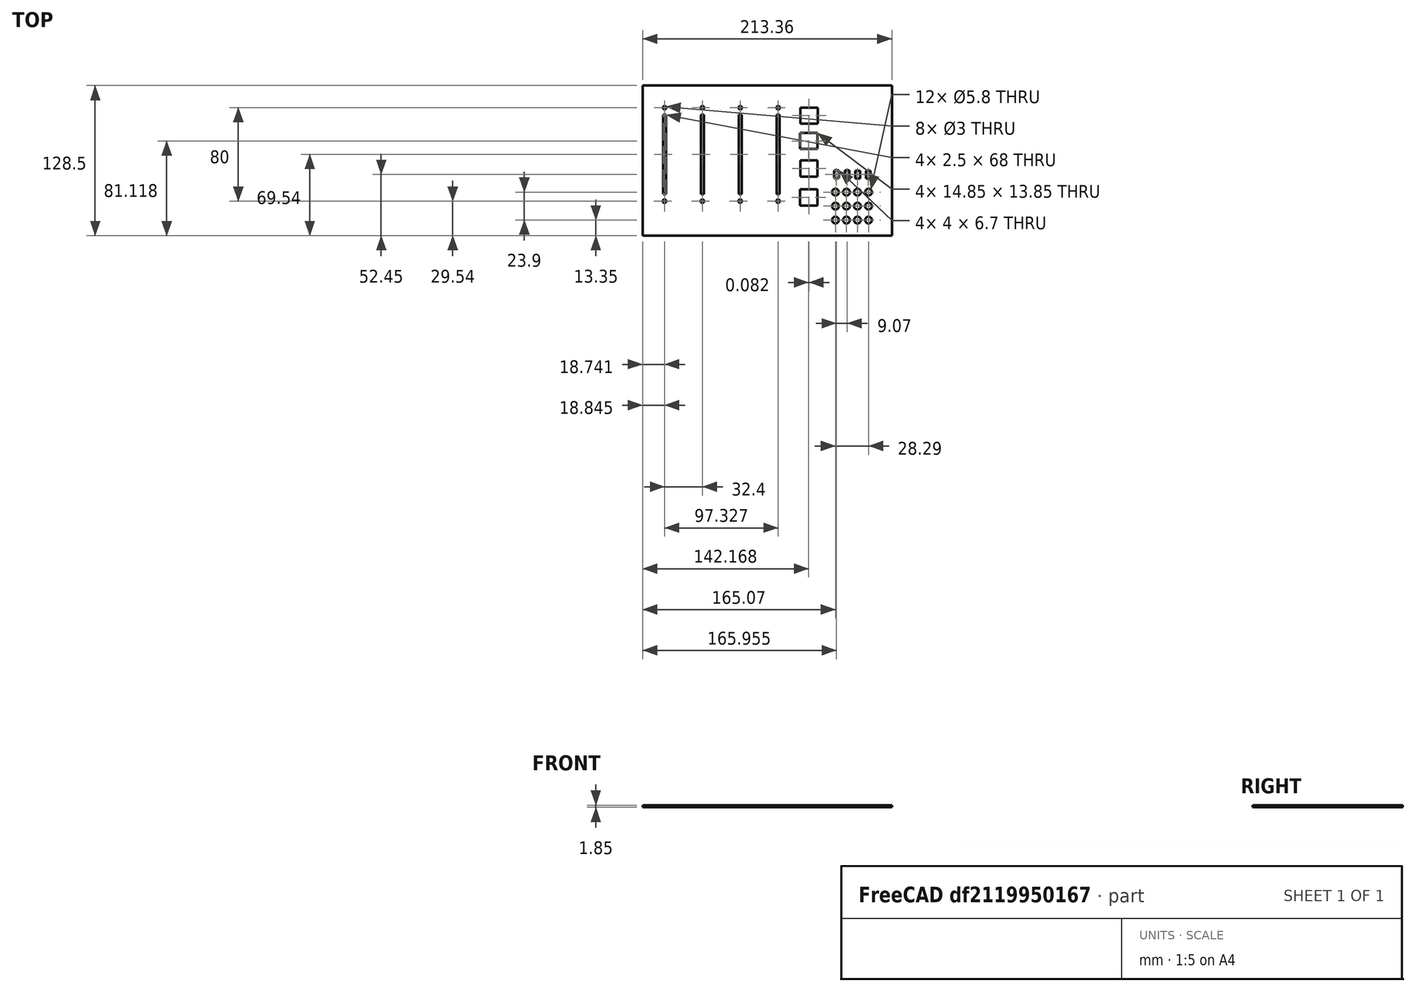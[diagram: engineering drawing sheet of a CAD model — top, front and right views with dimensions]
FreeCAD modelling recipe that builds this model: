
FCSTD DOCUMENT  (FreeCAD 0.19R24267 +148 (Git))
Label: FrontPanel
License: All rights reserved
LicenseURL: http://en.wikipedia.org/wiki/All_rights_reserved
objects: Sketcher::SketchObject×1, PartDesign::Pad×1, PartDesign::Body×1
note: 4 computed .brp shape members not serialized (recipe doc carries the construction recipe); baked Part::Feature solids carry a one-line shape summary decoded from their .brp

FEATURE [Sketcher::SketchObject] Sketch
  FullyConstrained = false
  MapMode = 5
  Support = -> [XY_Plane]
  sketch-geometry (93):
    g0: GeomPoint X=0 Y=0 Z=0
    g1: LineSegment StartX=0 StartY=0 StartZ=0 EndX=213.36 EndY=0 EndZ=0
    g2: LineSegment StartX=0 StartY=0 StartZ=0 EndX=0 EndY=128.5 EndZ=0
    g3: LineSegment StartX=0 StartY=128.5 StartZ=0 EndX=213.36 EndY=128.5 EndZ=0
    g4: LineSegment StartX=213.36 StartY=0 StartZ=0 EndX=213.36 EndY=128.5 EndZ=0
    g5: LineSegment StartX=17.5952 StartY=103.54 StartZ=0 EndX=20.0952 EndY=103.54 EndZ=0
    g6: LineSegment StartX=20.0952 StartY=103.54 StartZ=0 EndX=20.0952 EndY=35.54 EndZ=0
    g7: LineSegment StartX=20.0952 StartY=35.54 StartZ=0 EndX=17.5952 EndY=35.54 EndZ=0
    g8: LineSegment StartX=17.5952 StartY=35.54 StartZ=0 EndX=17.5952 EndY=103.54 EndZ=0
    g9: LineSegment StartX=49.9947 StartY=103.54 StartZ=0 EndX=52.4947 EndY=103.54 EndZ=0
    g10: LineSegment StartX=52.4947 StartY=103.54 StartZ=0 EndX=52.4947 EndY=35.54 EndZ=0
    g11: LineSegment StartX=52.4947 StartY=35.54 StartZ=0 EndX=49.9947 EndY=35.54 EndZ=0
    g12: LineSegment StartX=49.9947 StartY=35.54 StartZ=0 EndX=49.9947 EndY=103.54 EndZ=0
    g13: LineSegment StartX=17.5952 StartY=103.54 StartZ=0 EndX=49.9947 EndY=103.54 EndZ=0
    g14: LineSegment StartX=82.3943 StartY=103.54 StartZ=0 EndX=84.8943 EndY=103.54 EndZ=0
    g15: LineSegment StartX=84.8943 StartY=103.54 StartZ=0 EndX=84.8943 EndY=35.54 EndZ=0
    g16: LineSegment StartX=84.8943 StartY=35.54 StartZ=0 EndX=82.3943 EndY=35.54 EndZ=0
    g17: LineSegment StartX=82.3943 StartY=35.54 StartZ=0 EndX=82.3943 EndY=103.54 EndZ=0
    g18: LineSegment StartX=49.9947 StartY=103.54 StartZ=0 EndX=82.3943 EndY=103.54 EndZ=0
    g19: LineSegment StartX=114.794 StartY=103.54 StartZ=0 EndX=117.294 EndY=103.54 EndZ=0
    g20: LineSegment StartX=117.294 StartY=103.54 StartZ=0 EndX=117.294 EndY=35.54 EndZ=0
    g21: LineSegment StartX=117.294 StartY=35.54 StartZ=0 EndX=114.794 EndY=35.54 EndZ=0
    g22: LineSegment StartX=114.794 StartY=35.54 StartZ=0 EndX=114.794 EndY=103.54 EndZ=0
    g23: LineSegment StartX=82.3943 StartY=103.54 StartZ=0 EndX=114.794 EndY=103.54 EndZ=0
    g24: Circle CenterX=18.87 CenterY=109.54 CenterZ=0 NormalX=0 NormalY=0 NormalZ=1 AngleXU=0 Radius=1.5
    g25: Circle CenterX=18.7415 CenterY=29.54 CenterZ=0 NormalX=0 NormalY=0 NormalZ=1 AngleXU=0 Radius=1.5
    g26: Circle CenterX=51.141 CenterY=29.54 CenterZ=0 NormalX=0 NormalY=0 NormalZ=1 AngleXU=0 Radius=1.5
    g27: Circle CenterX=51.2695 CenterY=109.54 CenterZ=0 NormalX=0 NormalY=0 NormalZ=1 AngleXU=0 Radius=1.5
    g28: LineSegment StartX=18.7415 StartY=29.54 StartZ=0 EndX=51.141 EndY=29.54 EndZ=0
    g29: Circle CenterX=83.5405 CenterY=29.54 CenterZ=0 NormalX=0 NormalY=0 NormalZ=1 AngleXU=0 Radius=1.5
    g30: Circle CenterX=83.669 CenterY=109.54 CenterZ=0 NormalX=0 NormalY=0 NormalZ=1 AngleXU=0 Radius=1.5
    g31: LineSegment StartX=51.141 StartY=29.54 StartZ=0 EndX=83.5405 EndY=29.54 EndZ=0
    g32: Circle CenterX=115.94 CenterY=29.54 CenterZ=0 NormalX=0 NormalY=0 NormalZ=1 AngleXU=0 Radius=1.5
    g33: Circle CenterX=116.069 CenterY=109.54 CenterZ=0 NormalX=0 NormalY=0 NormalZ=1 AngleXU=0 Radius=1.5
    g34: LineSegment StartX=83.5405 StartY=29.54 StartZ=0 EndX=115.94 EndY=29.54 EndZ=0
    g35: Circle CenterX=165.07 CenterY=37.25 CenterZ=0 NormalX=0 NormalY=0 NormalZ=1 AngleXU=0 Radius=2.9
    g36: Circle CenterX=174.5 CenterY=37.25 CenterZ=0 NormalX=0 NormalY=0 NormalZ=1 AngleXU=0 Radius=2.9
    g37: LineSegment StartX=165.07 StartY=37.25 StartZ=0 EndX=174.5 EndY=37.25 EndZ=0
    g38: Circle CenterX=183.93 CenterY=37.25 CenterZ=0 NormalX=0 NormalY=0 NormalZ=1 AngleXU=0 Radius=2.9
    g39: LineSegment StartX=174.5 StartY=37.25 StartZ=0 EndX=183.93 EndY=37.25 EndZ=0
    g40: Circle CenterX=193.36 CenterY=37.25 CenterZ=0 NormalX=0 NormalY=0 NormalZ=1 AngleXU=0 Radius=2.9
    g41: LineSegment StartX=183.93 StartY=37.25 StartZ=0 EndX=193.36 EndY=37.25 EndZ=0
    g42: Circle CenterX=165.07 CenterY=25.3 CenterZ=0 NormalX=0 NormalY=0 NormalZ=1 AngleXU=0 Radius=2.9
    g43: LineSegment StartX=165.07 StartY=37.25 StartZ=0 EndX=165.07 EndY=25.3 EndZ=0
    g44: Circle CenterX=174.5 CenterY=25.3 CenterZ=0 NormalX=0 NormalY=0 NormalZ=1 AngleXU=0 Radius=2.9
    g45: LineSegment StartX=165.07 StartY=25.3 StartZ=0 EndX=174.5 EndY=25.3 EndZ=0
    g46: Circle CenterX=183.93 CenterY=25.3 CenterZ=0 NormalX=0 NormalY=0 NormalZ=1 AngleXU=0 Radius=2.9
    g47: LineSegment StartX=174.5 StartY=25.3 StartZ=0 EndX=183.93 EndY=25.3 EndZ=0
    g48: Circle CenterX=193.36 CenterY=25.3 CenterZ=0 NormalX=0 NormalY=0 NormalZ=1 AngleXU=0 Radius=2.9
    g49: LineSegment StartX=183.93 StartY=25.3 StartZ=0 EndX=193.36 EndY=25.3 EndZ=0
    g50: Circle CenterX=165.07 CenterY=13.35 CenterZ=0 NormalX=0 NormalY=0 NormalZ=1 AngleXU=0 Radius=2.9
    g51: LineSegment StartX=165.07 StartY=25.3 StartZ=0 EndX=165.07 EndY=13.35 EndZ=0
    g52: Circle CenterX=174.5 CenterY=13.35 CenterZ=0 NormalX=0 NormalY=0 NormalZ=1 AngleXU=0 Radius=2.9
    g53: LineSegment StartX=165.07 StartY=13.35 StartZ=0 EndX=174.5 EndY=13.35 EndZ=0
    g54: Circle CenterX=183.93 CenterY=13.35 CenterZ=0 NormalX=0 NormalY=0 NormalZ=1 AngleXU=0 Radius=2.9
    g55: LineSegment StartX=174.5 StartY=13.35 StartZ=0 EndX=183.93 EndY=13.35 EndZ=0
    g56: Circle CenterX=193.36 CenterY=13.35 CenterZ=0 NormalX=0 NormalY=0 NormalZ=1 AngleXU=0 Radius=2.9
    g57: LineSegment StartX=183.93 StartY=13.35 StartZ=0 EndX=193.36 EndY=13.35 EndZ=0
    g58: LineSegment StartX=163.955 StartY=55.8 StartZ=0 EndX=167.955 EndY=55.8 EndZ=0
    g59: LineSegment StartX=167.955 StartY=55.8 StartZ=0 EndX=167.955 EndY=49.1 EndZ=0
    g60: LineSegment StartX=167.955 StartY=49.1 StartZ=0 EndX=163.955 EndY=49.1 EndZ=0
    g61: LineSegment StartX=163.955 StartY=49.1 StartZ=0 EndX=163.955 EndY=55.8 EndZ=0
    g62: LineSegment StartX=173.025 StartY=55.7667 StartZ=0 EndX=177.025 EndY=55.7667 EndZ=0
    g63: LineSegment StartX=177.025 StartY=55.7667 StartZ=0 EndX=177.025 EndY=49.0667 EndZ=0
    g64: LineSegment StartX=177.025 StartY=49.0667 StartZ=0 EndX=173.025 EndY=49.0667 EndZ=0
    g65: LineSegment StartX=173.025 StartY=49.0667 StartZ=0 EndX=173.025 EndY=55.7667 EndZ=0
    g66: LineSegment StartX=163.955 StartY=55.8 StartZ=0 EndX=173.025 EndY=55.7667 EndZ=0
    g67: LineSegment StartX=182.095 StartY=55.7333 StartZ=0 EndX=186.095 EndY=55.7333 EndZ=0
    g68: LineSegment StartX=186.095 StartY=55.7333 StartZ=0 EndX=186.095 EndY=49.0333 EndZ=0
    g69: LineSegment StartX=186.095 StartY=49.0333 StartZ=0 EndX=182.095 EndY=49.0333 EndZ=0
    g70: LineSegment StartX=182.095 StartY=49.0333 StartZ=0 EndX=182.095 EndY=55.7333 EndZ=0
    g71: LineSegment StartX=173.025 StartY=55.7667 StartZ=0 EndX=182.095 EndY=55.7333 EndZ=0
    g72: LineSegment StartX=191.165 StartY=55.7 StartZ=0 EndX=195.165 EndY=55.7 EndZ=0
    g73: LineSegment StartX=195.165 StartY=55.7 StartZ=0 EndX=195.165 EndY=49 EndZ=0
    g74: LineSegment StartX=195.165 StartY=49 StartZ=0 EndX=191.165 EndY=49 EndZ=0
    g75: LineSegment StartX=191.165 StartY=49 StartZ=0 EndX=191.165 EndY=55.7 EndZ=0
    g76: LineSegment StartX=182.095 StartY=55.7333 StartZ=0 EndX=191.165 EndY=55.7 EndZ=0
    g77: LineSegment StartX=135.009 StartY=109.692 StartZ=0 EndX=149.859 EndY=109.692 EndZ=0
    g78: LineSegment StartX=149.859 StartY=109.692 StartZ=0 EndX=149.859 EndY=95.8422 EndZ=0
    g79: LineSegment StartX=149.859 StartY=95.8422 StartZ=0 EndX=135.009 EndY=95.8422 EndZ=0
    g80: LineSegment StartX=135.009 StartY=95.8422 StartZ=0 EndX=135.009 EndY=109.692 EndZ=0
    g81: LineSegment StartX=134.743 StartY=88.0435 StartZ=0 EndX=149.593 EndY=88.0435 EndZ=0
    g82: LineSegment StartX=149.593 StartY=88.0435 StartZ=0 EndX=149.593 EndY=74.1935 EndZ=0
    g83: LineSegment StartX=149.593 StartY=74.1935 StartZ=0 EndX=134.743 EndY=74.1935 EndZ=0
    g84: LineSegment StartX=134.743 StartY=74.1935 StartZ=0 EndX=134.743 EndY=88.0435 EndZ=0
    g85: LineSegment StartX=134.825 StartY=39.687 StartZ=0 EndX=149.675 EndY=39.687 EndZ=0
    g86: LineSegment StartX=149.675 StartY=39.687 StartZ=0 EndX=149.675 EndY=25.837 EndZ=0
    g87: LineSegment StartX=149.675 StartY=25.837 StartZ=0 EndX=134.825 EndY=25.837 EndZ=0
    g88: LineSegment StartX=134.825 StartY=25.837 StartZ=0 EndX=134.825 EndY=39.687 EndZ=0
    g89: LineSegment StartX=134.968 StartY=64.3578 StartZ=0 EndX=149.818 EndY=64.3578 EndZ=0
    g90: LineSegment StartX=149.818 StartY=64.3578 StartZ=0 EndX=149.818 EndY=50.5078 EndZ=0
    g91: LineSegment StartX=149.818 StartY=50.5078 StartZ=0 EndX=134.968 EndY=50.5078 EndZ=0
    g92: LineSegment StartX=134.968 StartY=50.5078 StartZ=0 EndX=134.968 EndY=64.3578 EndZ=0
  constraints (244):
    c: Coincident(g1,g-1)
    c: Horizontal(g1)
    c: DistanceX(g1,g1) = 213.36
    c: Coincident(g2,g1)
    c: PointOnObject(g2,g-2)
    c: DistanceY(g2,g2) = 128.5
    c: Coincident(g3,g2)
    c: Horizontal(g3)
    c: DistanceX(g3,g3) = 213.36
    c: Coincident(g4,g1)
    c: Coincident(g4,g3)
    c: Coincident(g5,g6)
    c: Coincident(g6,g7)
    c: Coincident(g7,g8)
    c: Coincident(g8,g5)
    c: Horizontal(g5)
    c: Horizontal(g7)
    c: Vertical(g6)
    c: Vertical(g8)
    c: DistanceX(g7,g7) = 2.5
    c: DistanceY(g6,g6) = 68
    c: Coincident(g9,g10)
    c: Coincident(g10,g11)
    c: Coincident(g11,g12)
    c: Coincident(g12,g9)
    c: Horizontal(g9)
    c: Horizontal(g11)
    c: Vertical(g10)
    c: Vertical(g12)
    c: DistanceX(g11,g11) = 2.5
    c: DistanceY(g10,g10) = 68
    c: Coincident(g5,g13)
    c: Coincident(g9,g13)
    c: Distance(g13) = 32.3995
    c: Angle(g13) = 0
    c: Coincident(g14,g15)
    c: Coincident(g15,g16)
    c: Coincident(g16,g17)
    c: Coincident(g17,g14)
    c: Horizontal(g14)
    c: Horizontal(g16)
    c: Vertical(g15)
    c: Vertical(g17)
    c: DistanceX(g16,g16) = 2.5
    c: DistanceY(g15,g15) = 68
    c: Coincident(g9,g18)
    c: Coincident(g14,g18)
    c: Equal(g13,g18)
    c: Parallel(g18,g13)
    c: Coincident(g19,g20)
    c: Coincident(g20,g21)
    c: Coincident(g21,g22)
    c: Coincident(g22,g19)
    c: Horizontal(g19)
    c: Horizontal(g21)
    c: Vertical(g20)
    c: Vertical(g22)
    c: DistanceX(g21,g21) = 2.5
    c: DistanceY(g20,g20) = 68
    c: Coincident(g14,g23)
    c: Coincident(g19,g23)
    c: Equal(g13,g23)
    c: Parallel(g23,g13)
    c: Radius(g24) = 1.5
    c: Equal(g24,g25) = 1.5
    c: DistanceY(g25,g24) = 80
    c: Radius(g27) = 1.5
    c: Equal(g27,g26) = 1.5
    c: DistanceY(g26,g27) = 80
    c: Coincident(g25,g28)
    c: Coincident(g26,g28)
    c: Distance(g28) = 32.3995
    c: Angle(g28) = 0
    c: Radius(g30) = 1.5
    c: Equal(g30,g29) = 1.5
    c: DistanceY(g29,g30) = 80
    c: Coincident(g26,g31)
    c: Coincident(g29,g31)
    c: Equal(g28,g31)
    c: Parallel(g31,g28)
    c: Radius(g33) = 1.5
    c: Equal(g33,g32) = 1.5
    c: DistanceY(g32,g33) = 80
    c: Coincident(g29,g34)
    c: Coincident(g32,g34)
    c: Equal(g28,g34)
    c: Parallel(g34,g28)
    c: Distance(g24,g5) = 6
    c: Distance(g27,g24) = 32.3995
    c: Distance(g27,g30) = 32.3995
    c: Distance(g33,g30) = 32.3995
    c: Distance(g30,g3) = 18.96
    c: Distance(g24,g2) = 18.87
    c: Radius(g35) = 2.9
    c: Radius(g36) = 2.9
    c: Coincident(g35,g37)
    c: Coincident(g36,g37)
    c: Distance(g37) = 9.43
    c: Angle(g37) = 0
    c: Radius(g38) = 2.9
    c: Coincident(g36,g39)
    c: Coincident(g38,g39)
    c: Equal(g37,g39)
    c: Parallel(g39,g37)
    c: Radius(g40) = 2.9
    c: Coincident(g38,g41)
    c: Coincident(g40,g41)
    c: Equal(g37,g41)
    c: Parallel(g41,g37)
    c: Radius(g42) = 2.9
    c: Coincident(g35,g43)
    c: Coincident(g42,g43)
    c: Distance(g43) = 11.95
    c: Perpendicular(g43,g37)
    c: Radius(g44) = 2.9
    c: Coincident(g42,g45)
    c: Coincident(g44,g45)
    c: Equal(g37,g45)
    c: Parallel(g45,g37)
    c: Radius(g46) = 2.9
    c: Coincident(g44,g47)
    c: Coincident(g46,g47)
    c: Equal(g37,g47)
    c: Parallel(g47,g37)
    c: Radius(g48) = 2.9
    c: Coincident(g46,g49)
    c: Coincident(g48,g49)
    c: Equal(g37,g49)
    c: Parallel(g49,g37)
    c: Radius(g50) = 2.9
    c: Coincident(g42,g51)
    c: Coincident(g50,g51)
    c: Equal(g43,g51)
    c: Perpendicular(g51,g37)
    c: Radius(g52) = 2.9
    c: Coincident(g50,g53)
    c: Coincident(g52,g53)
    c: Equal(g37,g53)
    c: Parallel(g53,g37)
    c: Radius(g54) = 2.9
    c: Coincident(g52,g55)
    c: Coincident(g54,g55)
    c: Equal(g37,g55)
    c: Parallel(g55,g37)
    c: Radius(g56) = 2.9
    c: Coincident(g54,g57)
    c: Coincident(g56,g57)
    c: Equal(g37,g57)
    c: Parallel(g57,g37)
    c: Coincident(g58,g59)
    c: Coincident(g59,g60)
    c: Coincident(g60,g61)
    c: Coincident(g61,g58)
    c: Horizontal(g58)
    c: Horizontal(g60)
    c: Vertical(g59)
    c: Vertical(g61)
    c: DistanceY(g59,g59) = 6.7
    c: DistanceX(g58,g58) = 4
    c: Coincident(g62,g63)
    c: Coincident(g63,g64)
    c: Coincident(g64,g65)
    c: Coincident(g65,g62)
    c: Horizontal(g62)
    c: Horizontal(g64)
    c: Vertical(g63)
    c: Vertical(g65)
    c: DistanceY(g63,g63) = 6.7
    c: DistanceX(g62,g62) = 4
    c: Coincident(g58,g66)
    c: Coincident(g62,g66)
    c: Distance(g66) = 9.07
    c: Angle(g66) = -0.00367502
    c: Coincident(g67,g68)
    c: Coincident(g68,g69)
    c: Coincident(g69,g70)
    c: Coincident(g70,g67)
    c: Horizontal(g67)
    c: Horizontal(g69)
    c: Vertical(g68)
    c: Vertical(g70)
    c: DistanceY(g68,g68) = 6.7
    c: DistanceX(g67,g67) = 4
    c: Coincident(g62,g71)
    c: Coincident(g67,g71)
    c: Equal(g66,g71)
    c: Parallel(g71,g66)
    c: Coincident(g72,g73)
    c: Coincident(g73,g74)
    c: Coincident(g74,g75)
    c: Coincident(g75,g72)
    c: Horizontal(g72)
    c: Horizontal(g74)
    c: Vertical(g73)
    c: Vertical(g75)
    c: DistanceY(g73,g73) = 6.7
    c: DistanceX(g72,g72) = 4
    c: Coincident(g67,g76)
    c: Coincident(g72,g76)
    c: Equal(g66,g76)
    c: Parallel(g76,g66)
    c: Distance(g35,g60) = 11.85
    c: Distance(g50,g1) = 13.35
    c: Distance(g48,g4) = 20
    c: Coincident(g77,g78)
    c: Coincident(g78,g79)
    c: Coincident(g79,g80)
    c: Coincident(g80,g77)
    c: Horizontal(g77)
    c: Horizontal(g79)
    c: Vertical(g78)
    c: Vertical(g80)
    c: DistanceX(g77,g77) = 14.85
    c: DistanceY(g78,g78) = 13.85
    c: Coincident(g81,g82)
    c: Coincident(g82,g83)
    c: Coincident(g83,g84)
    c: Coincident(g84,g81)
    c: Horizontal(g81)
    c: Horizontal(g83)
    c: Vertical(g82)
    c: Vertical(g84)
    c: Equal(g77,g81) = 14.85
    c: Equal(g78,g82) = 13.85
    c: Coincident(g89,g90)
    c: Coincident(g90,g91)
    c: Coincident(g91,g92)
    c: Coincident(g92,g89)
    c: Horizontal(g89)
    c: Horizontal(g91)
    c: Vertical(g90)
    c: Vertical(g92)
    c: Equal(g77,g89) = 14.85
    c: Equal(g78,g90) = 13.85
    c: Coincident(g85,g86)
    c: Coincident(g86,g87)
    c: Coincident(g87,g88)
    c: Coincident(g88,g85)
    c: Horizontal(g85)
    c: Horizontal(g87)
    c: Vertical(g86)
    c: Vertical(g88)
    c: Equal(g89,g85) = 14.85
    c: Equal(g90,g86) = 13.85
FEATURE [PartDesign::Pad] Pad
  Direction = (1,1,1)
  Length = 1.85
  Length2 = 100
  Profile = -> Sketch
  Type = 0
FEATURE [PartDesign::Body] Body
  Group = -> [Sketch,Pad]
  Origin = -> Origin
  Tip = -> Pad
